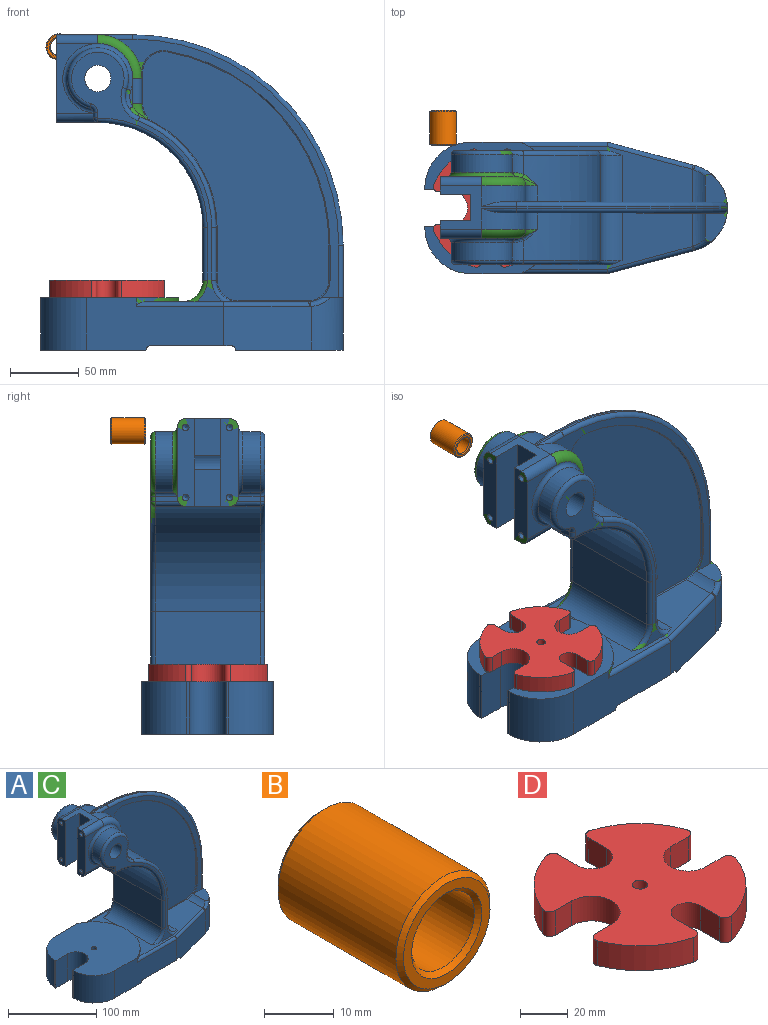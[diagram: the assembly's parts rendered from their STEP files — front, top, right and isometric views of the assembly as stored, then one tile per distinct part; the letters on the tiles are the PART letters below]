
ASSEMBLY  parts=4 mates=1
PART A: 180 faces, bbox 234.5x98.1x244 mm
  f0: plane 63.5x12.7mm, normal (-1,0,0), area 753.5mm2, adj f2,f15,f17,f92,f97,f149,f151,f158
  f1: plane 20.23x2.34mm, normal (0,1,0), area 23.9mm2, adj f90,f91,f104,f106
  f2: plane 50.8x30.1mm, normal (0,-1,0), area 515.4mm2, adj f0,f83,f92,f97,f124
  f3: plane 22.59x12.73mm, normal (1,0,0), area 235.4mm2, adj f19,f26,f32,f87,f94,f174
  f4: plane 22.59x12.73mm, normal (1,0,0), area 235.4mm2, adj f10,f14,f33,f86,f90,f164
  f5: plane 99.19x38.1mm, normal (0,-1,0), area 3202mm2, adj f6,f40,f46,f49,f52,f58,f76,f133
  f6: plane 100x95.25mm, normal (0,0,1), area 7398mm2, adj f5,f43,f44,f48,f54,f55,f56,f57
  f7: plane 38.1x34.96mm, normal (1,0,0), area 1331.9mm2, adj f8,f9,f114,f169
  f8: cylinder r=15.88mm len=34.96mm, axis (0,1,0), area 871.7mm2, adj f7,f37,f115,f167
  f9: cylinder r=85.72mm len=80.21mm, axis (0,1,0), area 3442.3mm2, adj f7,f80,f86,f100,f113,f168
  f10: cylinder r=15.88mm len=18.65mm, axis (0,1,0), area 22.7mm2, adj f4,f11,f33,f162
  f11: cylinder r=142.88mm len=140.67mm, axis (0,1,0), area 163.3mm2, adj f10,f12,f33,f160
  f12: plane 25.4x0.82mm, normal (-1,0,0), area 20.8mm2, adj f11,f13,f33,f161
  f13: cylinder r=15.88mm len=24.81mm, axis (0,1,0), area 242.1mm2, adj f12,f33,f37,f45,f139,f140,f163
  f14: cylinder r=31.75mm len=31.75mm, axis (0,1,0), area 616.8mm2, adj f4,f15,f33,f89,f141
  f15: plane 55.5x31.75mm, normal (0,0,1), area 573.2mm2, adj f0,f14,f16,f19,f31,f88,f92,f141
  f16: plane 63.5x12.7mm, normal (-1,0,0), area 753.5mm2, adj f15,f17,f21,f88,f96,f147,f153,f157
  f17: plane 31.75x30.1mm, normal (0,0,-1), area 533.2mm2, adj f0,f16,f18,f96,f97,f156,f157,f158
  f18: cylinder r=76.2mm len=76.2mm, axis (0,1,0), area 9120.7mm2, adj f17,f22,f103,f105,f119,f121
  f19: cylinder r=31.75mm len=31.75mm, axis (0,1,0), area 616.8mm2, adj f3,f15,f32,f93,f144
  f20: plane 20.23x2.34mm, normal (0,-1,0), area 23.9mm2, adj f94,f95,f122,f124
  f21: plane 50.8x30.1mm, normal (0,1,0), area 515.4mm2, adj f16,f78,f88,f96,f106
  f22: plane 76.2x38.1mm, normal (-1,0,0), area 2903.2mm2, adj f18,f98,f101,f117
  f23: cylinder r=15.88mm len=34.96mm, axis (0,1,0), area 871.7mm2, adj f24,f37,f132,f177
  f24: plane 38.1x34.96mm, normal (1,0,0), area 1331.9mm2, adj f23,f25,f131,f179
  f25: cylinder r=85.72mm len=80.21mm, axis (0,1,0), area 3442.3mm2, adj f24,f81,f87,f118,f130,f178
  f26: cylinder r=15.88mm len=18.65mm, axis (0,1,0), area 22.7mm2, adj f3,f27,f32,f172
  f27: cylinder r=142.88mm len=140.67mm, axis (0,1,0), area 163.3mm2, adj f26,f28,f32,f170
  f28: plane 25.4x0.82mm, normal (-1,0,0), area 20.8mm2, adj f27,f29,f32,f171
  f29: cylinder r=15.88mm len=24.81mm, axis (0,1,0), area 242.1mm2, adj f28,f32,f36,f37,f135,f136,f173
  f30: plane 76.2x7.92mm, normal (1,0,0), area 361.9mm2, adj f31,f36,f42,f45,f51,f53,f143,f146
  f31: cylinder r=152.4mm len=152.4mm, axis (0,1,0), area 377mm2, adj f15,f30,f142,f145
  f32: plane 187.33x160.79mm, normal (0,-1,0), area 1900.4mm2, adj f3,f19,f26,f27,f28,f29,f36,f144
  f33: plane 187.33x160.79mm, normal (0,1,0), area 1900.4mm2, adj f4,f10,f11,f12,f13,f14,f45,f141
  f34: plane 180.67x135mm, normal (0,-1,0), area 14138.8mm2, adj f170,f171,f172,f173,f174,f175,f176,f177
  f35: plane 180.67x135mm, normal (0,1,0), area 14138.8mm2, adj f160,f161,f162,f163,f164,f165,f166,f167
  f36: plane 26.58x18.73mm, normal (0,0,1), area 245.8mm2, adj f29,f30,f32,f53,f136,f146
  f37: plane 119.12x89.67mm, normal (0,0,1), area 4280.2mm2, adj f8,f13,f23,f29,f76,f77,f84,f98
  f38: cylinder r=3.17mm len=9.06mm, axis (0,1,0), area 40.9mm2, adj f40,f42,f52,f69
  f39: cylinder r=3.17mm len=7.93mm, axis (0,1,0), area 39.5mm2, adj f41,f46,f48,f65
  f40: plane 58.73x9.7mm, normal (0,0,-1), area 467.1mm2, adj f5,f38,f49,f52,f64,f69
  f41: plane 58.73x9.7mm, normal (0,0,-1), area 467.1mm2, adj f39,f47,f48,f50,f65,f67
  f42: plane 90.55x77.8mm, normal (0,0,-1), area 1454mm2, adj f30,f38,f47,f50,f51,f52,f53,f59
  f43: plane 38.1x1.61mm, normal (-1,0,0), area 61.5mm2, adj f6,f46,f54,f58
  f44: plane 38.1x1.61mm, normal (-1,0,0), area 61.5mm2, adj f6,f46,f55,f57
  f45: plane 26.58x18.73mm, normal (0,0,1), area 245.8mm2, adj f13,f30,f33,f51,f140,f143
  f46: plane 95.25x76.2mm, normal (0,0,-1), area 2029.8mm2, adj f5,f39,f43,f44,f48,f49,f54,f55
  f47: cylinder r=3.17mm len=9.06mm, axis (0,1,0), area 40.9mm2, adj f41,f42,f50,f67
  f48: plane 99.19x38.1mm, normal (0,1,0), area 3202mm2, adj f6,f39,f41,f46,f50,f57,f76,f137
  f49: cylinder r=3.17mm len=7.93mm, axis (0,1,0), area 39.5mm2, adj f5,f40,f46,f64
  f50: plane 63.64x32.15mm, normal (0.26,0.97,0), area 2053.6mm2, adj f41,f42,f47,f48,f51,f138,f139
  f51: cylinder r=31.75mm len=38.1mm, axis (0,0,-1), area 1379.2mm2, adj f30,f42,f45,f50,f140
  f52: plane 63.64x32.15mm, normal (0.26,-0.97,0), area 2053.6mm2, adj f5,f38,f40,f42,f53,f134,f135
  f53: cylinder r=31.75mm len=38.1mm, axis (0,0,-1), area 1379.2mm2, adj f30,f36,f42,f52,f136
  f54: plane 38.1x19.05mm, normal (0,1,0), area 725.8mm2, adj f6,f43,f46,f56
  f55: plane 38.1x19.05mm, normal (0,-1,0), area 725.8mm2, adj f6,f44,f46,f56
  f56: cylinder r=13.49mm len=38.1mm, axis (0,0,-1), area 1615.1mm2, adj f6,f46,f54,f55
  f57: cylinder r=33.32mm len=38.1mm, axis (0,0,-1), area 1963.7mm2, adj f6,f44,f46,f48
  f58: cylinder r=33.32mm len=38.1mm, axis (0,0,-1), area 1963.7mm2, adj f5,f6,f43,f46
  f59: plane 30.18x6.86mm, normal (-1,0,0), area 207mm2, adj f42,f60,f68,f70
  f60: plane 31.27x5.6mm, normal (0,0,-1), area 124.1mm2, adj f59,f61,f68,f70
  f61: cylinder r=23.8mm len=46.06mm, axis (0,1,0), area 499.2mm2, adj f60,f62,f67,f68,f69,f70
  f62: plane 84.13x79.4mm, normal (0,0,-1), area 5642.5mm2, adj f61,f64,f65,f66,f67,f69
  f63: plane 100.62x79.4mm, normal (0,0,-1), area 6568.5mm2, adj f64,f65,f66,f71,f72,f73,f74,f75
  f64: plane 98.15x30.18mm, normal (0,1,0), area 2718.8mm2, adj f40,f46,f49,f62,f63,f66,f69,f75
  f65: plane 98.15x30.18mm, normal (0,-1,0), area 2718.8mm2, adj f39,f41,f46,f62,f63,f66,f67,f74
  f66: plane 79.4x3.18mm, normal (-1,0,0), area 252.1mm2, adj f62,f63,f64,f65
  f67: plane 62.63x27.36mm, normal (-0.26,-0.97,0), area 1710.8mm2, adj f41,f42,f47,f61,f62,f65,f68
  f68: cylinder r=23.83mm len=30.18mm, axis (0,0,-1), area 814.8mm2, adj f42,f59,f60,f61,f67
  f69: plane 62.63x27.36mm, normal (-0.26,0.97,0), area 1710.8mm2, adj f38,f40,f42,f61,f62,f64,f70
  f70: cylinder r=23.83mm len=30.18mm, axis (0,0,-1), area 814.8mm2, adj f42,f59,f60,f61,f69
  f71: plane 30.18x10.12mm, normal (0,-1,0), area 305.3mm2, adj f46,f63,f73,f75
  f72: plane 30.18x10.12mm, normal (0,1,0), area 305.3mm2, adj f46,f63,f73,f74
  f73: cylinder r=21.42mm len=42.84mm, axis (0,0,-1), area 2030.4mm2, adj f46,f63,f71,f72
  f74: cylinder r=25.4mm len=30.18mm, axis (0,0,-1), area 986.2mm2, adj f46,f63,f65,f72
  f75: cylinder r=25.4mm len=30.18mm, axis (0,0,-1), area 986.2mm2, adj f46,f63,f64,f71
  f76: cylinder r=52.37mm len=95.25mm, axis (0,0,1), area 401mm2, adj f5,f6,f37,f48,f133,f137
  f77: plane 180.98x110.12mm, normal (0,1,0), area 1717.8mm2, adj f37,f85,f99,f101,f103,f109,f110,f111
  f78: plane 16.73x3.98mm, normal (-1,0,0), area 64.1mm2, adj f21,f96,f105,f106,f108,f109
  f79: cylinder r=22.23mm len=44.45mm, axis (0,1,0), area 1356.2mm2, adj f80,f106,f108,f111
  f80: cylinder r=15.88mm len=20.22mm, axis (0,1,0), area 319.4mm2, adj f9,f79,f102,f104,f112
  f81: cylinder r=15.88mm len=20.22mm, axis (0,1,0), area 319.4mm2, adj f25,f82,f120,f122,f129
  f82: cylinder r=22.23mm len=44.45mm, axis (0,1,0), area 1356.2mm2, adj f81,f124,f126,f128
  f83: plane 16.73x3.98mm, normal (-1,0,0), area 64.1mm2, adj f2,f97,f121,f124,f125,f126
  f84: plane 180.98x110.12mm, normal (0,-1,0), area 1717.8mm2, adj f37,f85,f116,f117,f119,f125,f127,f128
  f85: cylinder r=9.53mm len=82.55mm, axis (0,1,0), area 4727mm2, adj f77,f84,f156,f157,f158,f159
  f86: cylinder r=15.88mm len=14.02mm, axis (0,1,0), area 218.9mm2, adj f4,f9,f91,f166
  f87: cylinder r=15.88mm len=14.02mm, axis (0,1,0), area 218.9mm2, adj f3,f25,f95,f176
  f88: cylinder r=6.35mm len=30.1mm, axis (-1,0,0), area 300.2mm2, adj f15,f16,f21,f89
  f89: torus R=25.4mm, axis (0,-1,0), area 461.3mm2, adj f14,f88,f90,f106
  f90: cylinder r=6.35mm len=18.2mm, axis (0,0,1), area 181.6mm2, adj f1,f4,f89,f91
  f91: torus R=22.23mm, axis (0,-1,0), area 98mm2, adj f1,f86,f90,f100,f102
  f92: cylinder r=6.35mm len=30.1mm, axis (1,0,0), area 300.2mm2, adj f0,f2,f15,f93
  f93: torus R=25.4mm, axis (0,-1,0), area 461.3mm2, adj f19,f92,f94,f124
  f94: cylinder r=6.35mm len=18.2mm, axis (0,0,-1), area 181.6mm2, adj f3,f20,f93,f95
  f95: torus R=22.23mm, axis (0,-1,0), area 98mm2, adj f20,f87,f94,f118,f120
  f96: cylinder r=6.35mm len=30.1mm, axis (1,0,0), area 279.1mm2, adj f16,f17,f21,f78,f105
  f97: cylinder r=6.35mm len=30.1mm, axis (-1,0,0), area 279.1mm2, adj f0,f2,f17,f83,f121
  f98: cylinder r=15.88mm len=76.2mm, axis (0,-1,0), area 1900.2mm2, adj f22,f37,f99,f116
  f99: torus R=19.05mm, axis (0,-1,0), area 107.7mm2, adj f37,f77,f98,f101
  f100: bspline ~12.01x8.85mm, area 17.9mm2, adj f9,f91,f102
  f101: cylinder r=3.17mm len=38.1mm, axis (0,0,-1), area 190mm2, adj f22,f77,f99,f103
  f102: bspline ~10.6x9.56mm, area 36.6mm2, adj f80,f91,f100,f104
  f103: torus R=79.38mm, axis (0,-1,0), area 606mm2, adj f18,f77,f101,f107
  f104: torus R=12.7mm, axis (0,-1,0), area 70.6mm2, adj f1,f80,f102,f106
  f105: cylinder r=3.17mm len=22.23mm, axis (0,1,0), area 97.1mm2, adj f18,f78,f96,f107
  f106: torus R=25.4mm, axis (0,-1,0), area 570mm2, adj f1,f21,f78,f79,f89,f104,f108
  f107: sphere r=3.17mm, area 21.6mm2, adj f103,f105,f109
  f108: cylinder r=3.17mm len=15.82mm, axis (0,1,0), area 59.7mm2, adj f78,f79,f106,f110
  f109: cylinder r=3.17mm len=3.98mm, axis (0,0,-1), area 19.9mm2, adj f77,f78,f107,f110
  f110: torus R=6.35mm, axis (0,-1,0), area 28.5mm2, adj f77,f108,f109,f111
  f111: torus R=19.05mm, axis (0,-1,0), area 504.9mm2, adj f77,f79,f110,f112
  f112: torus R=19.05mm, axis (0,-1,0), area 132.1mm2, adj f77,f80,f111,f113
  f113: torus R=82.55mm, axis (0,-1,0), area 510.4mm2, adj f9,f77,f112,f114
  f114: cylinder r=3.17mm len=38.1mm, axis (0,0,1), area 190mm2, adj f7,f77,f113,f115
  f115: torus R=19.05mm, axis (0,-1,0), area 107.7mm2, adj f8,f37,f77,f114
  f116: torus R=19.05mm, axis (0,-1,0), area 107.7mm2, adj f37,f84,f98,f117
  f117: cylinder r=3.17mm len=38.1mm, axis (0,0,1), area 190mm2, adj f22,f84,f116,f119
  f118: bspline ~11.06x8.44mm, area 17.9mm2, adj f25,f95,f120
  f119: torus R=79.38mm, axis (0,-1,0), area 606mm2, adj f18,f84,f117,f123
  f120: bspline ~9.12x8.99mm, area 36.6mm2, adj f81,f95,f118,f122
  f121: cylinder r=3.17mm len=22.23mm, axis (0,1,0), area 97.1mm2, adj f18,f83,f97,f123
  f122: torus R=12.7mm, axis (0,-1,0), area 70.6mm2, adj f20,f81,f120,f124
  f123: sphere r=3.17mm, area 15.8mm2, adj f119,f121,f125
  f124: torus R=25.4mm, axis (0,-1,0), area 570mm2, adj f2,f20,f82,f83,f93,f122,f126
  f125: cylinder r=3.17mm len=3.98mm, axis (0,0,1), area 19.9mm2, adj f83,f84,f123,f127
  f126: cylinder r=3.17mm len=15.82mm, axis (0,1,0), area 59.7mm2, adj f82,f83,f124,f127
  f127: torus R=6.35mm, axis (0,-1,0), area 28.5mm2, adj f84,f125,f126,f128
  f128: torus R=19.05mm, axis (0,-1,0), area 504.9mm2, adj f82,f84,f127,f129
  f129: torus R=19.05mm, axis (0,-1,0), area 132.1mm2, adj f81,f84,f128,f130
  f130: torus R=82.55mm, axis (0,-1,0), area 510.4mm2, adj f25,f84,f129,f131
  f131: cylinder r=3.17mm len=38.1mm, axis (0,0,-1), area 190mm2, adj f24,f84,f130,f132
  f132: torus R=19.05mm, axis (0,-1,0), area 107.7mm2, adj f23,f37,f84,f131
  f133: cylinder r=3.17mm len=63.09mm, axis (1,0,0), area 298.9mm2, adj f5,f37,f76,f134
  f134: cylinder r=3.17mm len=62.81mm, axis (0.97,0.26,0), area 319mm2, adj f37,f52,f133,f135
  f135: bspline ~3.41x3.21mm, area 6mm2, adj f29,f52,f134,f136
  f136: bspline ~18.95x11.92mm, area 79.7mm2, adj f29,f36,f53,f135
  f137: cylinder r=3.17mm len=63.09mm, axis (-1,0,0), area 298.9mm2, adj f37,f48,f76,f138
  f138: cylinder r=3.17mm len=62.81mm, axis (-0.97,0.26,0), area 319mm2, adj f37,f50,f137,f139
  f139: bspline ~6.89x4.84mm, area 6mm2, adj f13,f50,f138,f140
  f140: bspline ~17.46x11.57mm, area 79.7mm2, adj f13,f45,f51,f139
  f141: cylinder r=3.17mm len=25.4mm, axis (-1,0,0), area 92.2mm2, adj f14,f15,f33,f142
  f142: torus R=149.22mm, axis (0,-1,0), area 1184.9mm2, adj f31,f33,f141,f143
  f143: cylinder r=3.17mm len=38.1mm, axis (0,0,1), area 190mm2, adj f30,f33,f45,f142
  f144: cylinder r=3.17mm len=25.4mm, axis (1,0,0), area 92.2mm2, adj f15,f19,f32,f145
  f145: torus R=149.22mm, axis (0,-1,0), area 1184.9mm2, adj f31,f32,f144,f146
  f146: cylinder r=3.17mm len=38.1mm, axis (0,0,-1), area 190mm2, adj f30,f32,f36,f145
  f147: cylinder r=2.38mm len=12.7mm, axis (-1,0,0), area 190mm2, adj f16,f148
  f148: cone r=0mm half-angle=59deg, axis (-1,0,0), area 20.8mm2, adj f147
  f149: cylinder r=2.38mm len=12.7mm, axis (-1,0,0), area 190mm2, adj f0,f150
  f150: cone r=0mm half-angle=59deg, axis (-1,0,0), area 20.8mm2, adj f149
  f151: cylinder r=2.38mm len=12.7mm, axis (-1,0,0), area 190mm2, adj f0,f152
  f152: cone r=0mm half-angle=59deg, axis (-1,0,0), area 20.8mm2, adj f151
  f153: cylinder r=2.38mm len=12.7mm, axis (-1,0,0), area 190mm2, adj f16,f154
  f154: cone r=0mm half-angle=59deg, axis (-1,0,0), area 20.8mm2, adj f153
  f155: cylinder r=3.17mm len=7.93mm, axis (0,0,1), area 158.1mm2, adj f6,f63
  f156: plane 26.47x19.05mm, normal (-1,0,0), area 504.2mm2, adj f17,f85,f157,f158
  f157: plane 63.5x22.17mm, normal (0,-1,0), area 1396.6mm2, adj f15,f16,f17,f85,f156,f159
  f158: plane 63.5x22.17mm, normal (0,1,0), area 1396.6mm2, adj f0,f15,f17,f85,f156,f159
  f159: plane 26.47x19.05mm, normal (-1,0,0), area 504.2mm2, adj f15,f85,f157,f158
  f160: torus R=142.11mm, axis (0,-1,0), area 238.1mm2, adj f11,f35,f161,f162
  f161: cylinder r=0.76mm len=25.4mm, axis (0,0,1), area 30.4mm2, adj f12,f35,f160,f163
  f162: torus R=15.11mm, axis (0,-1,0), area 32.6mm2, adj f10,f35,f160,f164
  f163: torus R=15.11mm, axis (0,-1,0), area 29.3mm2, adj f13,f35,f161,f165
  f164: cylinder r=0.76mm len=22.59mm, axis (0,0,1), area 27mm2, adj f4,f35,f162,f166
  f165: cylinder r=0.76mm len=50.8mm, axis (1,0,0), area 60.8mm2, adj f35,f37,f163,f167
  f166: torus R=15.11mm, axis (0,-1,0), area 20.2mm2, adj f35,f86,f164,f168
  f167: torus R=15.11mm, axis (0,-1,0), area 29.3mm2, adj f8,f35,f165,f169
  f168: torus R=86.49mm, axis (0,-1,0), area 111.5mm2, adj f9,f35,f166,f169
  f169: cylinder r=0.76mm len=38.1mm, axis (0,0,-1), area 45.6mm2, adj f7,f35,f167,f168
  f170: torus R=142.11mm, axis (0,-1,0), area 238.1mm2, adj f27,f34,f171,f172
  f171: cylinder r=0.76mm len=25.4mm, axis (0,0,-1), area 30.4mm2, adj f28,f34,f170,f173
  f172: torus R=15.11mm, axis (0,-1,0), area 32.6mm2, adj f26,f34,f170,f174
  f173: torus R=15.11mm, axis (0,-1,0), area 29.3mm2, adj f29,f34,f171,f175
  f174: cylinder r=0.76mm len=22.59mm, axis (0,0,-1), area 27mm2, adj f3,f34,f172,f176
  f175: cylinder r=0.76mm len=50.8mm, axis (-1,0,0), area 60.8mm2, adj f34,f37,f173,f177
  f176: torus R=15.11mm, axis (0,-1,0), area 20.2mm2, adj f34,f87,f174,f178
  f177: torus R=15.11mm, axis (0,-1,0), area 29.3mm2, adj f23,f34,f175,f179
  f178: torus R=86.49mm, axis (0,-1,0), area 111.5mm2, adj f25,f34,f176,f179
  f179: cylinder r=0.76mm len=38.1mm, axis (0,0,1), area 45.6mm2, adj f24,f34,f177,f178
PART B: 8 faces, bbox 19.1x25.4x19.1 mm
  f0: plane 17.53x17.53mm, normal (0,-1,0), area 82.3mm2, adj f4,f5
  f1: plane 17.53x17.53mm, normal (0,1,0), area 82.3mm2, adj f6,f7
  f2: cylinder r=9.53mm len=23.88mm, axis (0,1,0), area 1428.9mm2, adj f4,f7
  f3: cylinder r=6.35mm len=23.88mm, axis (0,1,0), area 952.6mm2, adj f5,f6
  f4: cone r=9.53mm half-angle=45deg, axis (0,1,0), area 61.9mm2, adj f0,f2
  f5: cone r=6.35mm half-angle=45deg, axis (0,-1,0), area 45.6mm2, adj f0,f3
  f6: cone r=6.35mm half-angle=45deg, axis (0,1,0), area 45.6mm2, adj f1,f3
  f7: cone r=9.53mm half-angle=45deg, axis (0,-1,0), area 61.9mm2, adj f1,f2
PART C: same geometry as A
PART D: 27 faces, bbox 83.8x85.8x12.7 mm
  f0: cylinder r=44.45mm len=28.56mm, axis (0,0,-1), area 510.6mm2, adj f17,f18,f19,f25
  f1: plane 12.7x9.85mm, normal (0,-1,0), area 125.1mm2, adj f2,f17,f18,f25
  f2: cylinder r=11.9mm len=23.8mm, axis (0,0,-1), area 474.8mm2, adj f1,f3,f17,f18
  f3: plane 12.7x9.85mm, normal (0,1,0), area 125.1mm2, adj f2,f17,f18,f26
  f4: cylinder r=44.45mm len=30.27mm, axis (0,0,-1), area 533.1mm2, adj f17,f18,f20,f26
  f5: plane 12.7x11.39mm, normal (1,0,0), area 144.7mm2, adj f6,f17,f18,f20
  f6: cylinder r=7.14mm len=14.28mm, axis (0,0,-1), area 284.8mm2, adj f5,f7,f17,f18
  f7: plane 12.7x11.39mm, normal (-1,0,0), area 144.7mm2, adj f6,f17,f18,f21
  f8: cylinder r=44.45mm len=30.9mm, axis (0,0,-1), area 556.3mm2, adj f17,f18,f21,f22
  f9: plane 12.7x10.43mm, normal (0,1,0), area 132.5mm2, adj f10,f17,f18,f22
  f10: cylinder r=10.31mm len=20.62mm, axis (0,0,-1), area 411.4mm2, adj f9,f11,f17,f18
  f11: plane 12.7x10.43mm, normal (0,-1,0), area 132.5mm2, adj f10,f17,f18,f23
  f12: cylinder r=44.45mm len=29.19mm, axis (0,0,-1), area 533.7mm2, adj f17,f18,f23,f24
  f13: plane 12.7x10.95mm, normal (-1,0,0), area 139mm2, adj f14,f17,f18,f24
  f14: cylinder r=8.72mm len=17.45mm, axis (0,0,-1), area 348.1mm2, adj f13,f15,f17,f18
  f15: plane 12.7x10.95mm, normal (1,0,0), area 139mm2, adj f14,f17,f18,f19
  f16: cylinder r=3.17mm len=12.7mm, axis (0,0,-1), area 253.4mm2, adj f17,f18
  f17: plane 85.84x83.78mm, normal (0,0,1), area 4373.8mm2, adj f0,f1,f2,f3,f4,f5,f6,f7
  f18: plane 85.84x83.78mm, normal (0,0,-1), area 4373.8mm2, adj f0,f1,f2,f3,f4,f5,f6,f7
  f19: cylinder r=3.17mm len=12.7mm, axis (0,0,-1), area 75.1mm2, adj f0,f15,f17,f18
  f20: cylinder r=3.17mm len=12.7mm, axis (0,0,-1), area 73.5mm2, adj f4,f5,f17,f18
  f21: cylinder r=3.17mm len=12.7mm, axis (0,0,-1), area 73.5mm2, adj f7,f8,f17,f18
  f22: cylinder r=3.17mm len=12.7mm, axis (0,0,-1), area 76.8mm2, adj f8,f9,f17,f18
  f23: cylinder r=3.17mm len=12.7mm, axis (0,0,-1), area 76.8mm2, adj f11,f12,f17,f18
  f24: cylinder r=3.17mm len=12.7mm, axis (0,0,-1), area 75.1mm2, adj f12,f13,f17,f18
  f25: cylinder r=3.17mm len=12.7mm, axis (0,0,-1), area 78.4mm2, adj f0,f1,f17,f18
  f26: cylinder r=3.17mm len=12.7mm, axis (0,0,-1), area 78.4mm2, adj f3,f4,f17,f18
PLACE A at identity
PLACE B t=(-28.03,29.12,22.87)mm
PLACE C at identity
PLACE D at identity
MATE fastened D.f16 <-> A.f76  axis (0,0,-1) through (6.35,0,-158.75)mm
